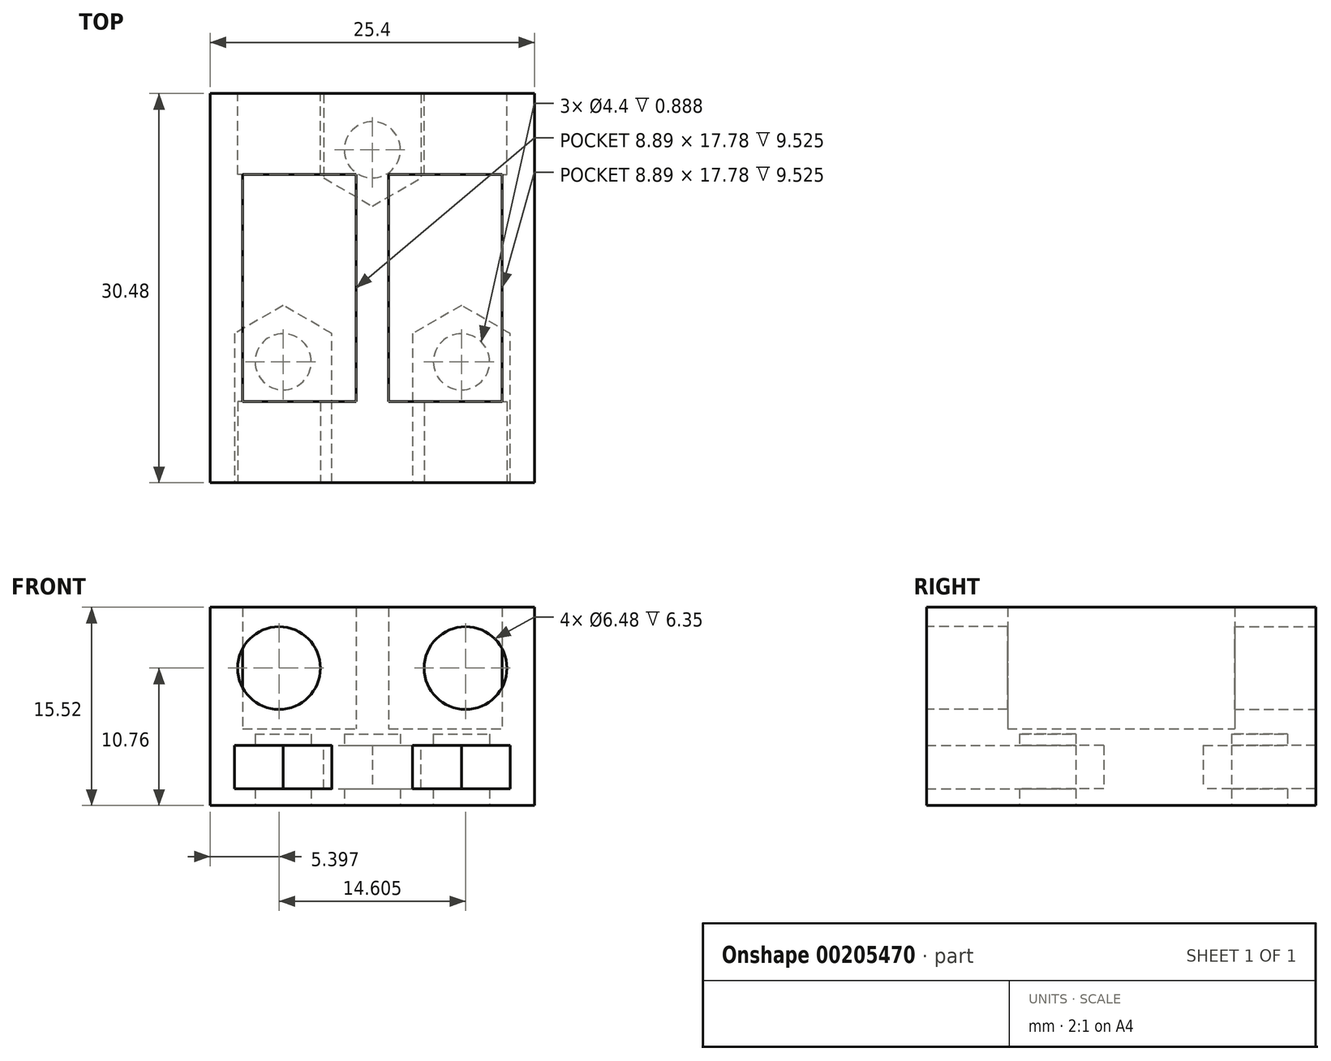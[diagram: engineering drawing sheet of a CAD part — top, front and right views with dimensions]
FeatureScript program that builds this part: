
annotation { "Feature Type Name" : "Feature", "Feature Type Description" : "" }
export const myFeature = defineFeature(function(context is Context, id is Id, definition is map)
    precondition{}
    {
        {
            var Q0;
            Q0=qCreatedBy(makeId("Front.planeOp"),FACE);
            var sketch = newSketch(context, id + "F0", { "sketchPlane" : qUnion([Q0])});
            skLineSegment(sketch, "E0.bottom", {"start": v(12.7, 4.76) * mm, "end": v(-12.7, 4.76) * mm});
            skLineSegment(sketch, "E0.top", {"start": v(12.7, -4.76) * mm, "end": v(-12.7, -4.76) * mm});
            skLineSegment(sketch, "E0.left", {"start": v(12.7, 4.76) * mm, "end": v(12.7, -4.76) * mm});
            skLineSegment(sketch, "E0.right", {"start": v(-12.7, 4.76) * mm, "end": v(-12.7, -4.76) * mm});
            skPoint(sketch, "E0.middle", {"position": v(0, 0) * mm});
            skSolve(sketch);
        }
        {
            var Q0;
            Q0=makeQuery(id+"F0.imprint","IMPRINT",FACE,{"disambiguationData":[TD([[makeQuery(id+"F0.imprint","IMPRINT",EDGE,{"derivedFrom":sQuery(id+"F0.wireOp",EDGE,"E0.bottom")}),1.0]])]});
            extrude(context, id + "F1", {"entities" : qUnion([Q0]), "depth" : 6.35 * mm});
        }
        {
            var Q0;
            Q0=makeQuery(id+"F1.opExtrude","CAP_FACE",FACE,{"disambiguationData":[OSD([sQuery(id+"F0.wireOp",EDGE,"E0.bottom"),sQuery(id+"F0.wireOp",EDGE,"E0.top"),sQuery(id+"F0.wireOp",EDGE,"E0.left"),sQuery(id+"F0.wireOp",EDGE,"E0.right")])],"isStart":false});
            var sketch = newSketch(context, id + "F2", { "sketchPlane" : qUnion([Q0])});
            skLineSegment(sketch, "E1.bottom", {"start": v(-12.7, 4.76) * mm, "end": v(-10.16, 4.76) * mm});
            skLineSegment(sketch, "E1.top", {"start": v(-12.7, -4.76) * mm, "end": v(-10.16, -4.76) * mm});
            skLineSegment(sketch, "E1.left", {"start": v(-12.7, 4.76) * mm, "end": v(-12.7, -4.76) * mm});
            skLineSegment(sketch, "E1.right", {"start": v(-10.16, 4.76) * mm, "end": v(-10.16, -4.76) * mm});
            skLineSegment(sketch, "E2.bottom", {"start": v(1.27, 4.76) * mm, "end": v(-1.27, 4.76) * mm});
            skLineSegment(sketch, "E2.top", {"start": v(1.27, -4.76) * mm, "end": v(-1.27, -4.76) * mm});
            skLineSegment(sketch, "E2.left", {"start": v(1.27, 4.76) * mm, "end": v(1.27, -4.76) * mm});
            skLineSegment(sketch, "E2.right", {"start": v(-1.27, 4.76) * mm, "end": v(-1.27, -4.76) * mm});
            skPoint(sketch, "E2.middle", {"position": v(0, 0) * mm});
            skLineSegment(sketch, "E3", {"start": v(0, 4.76) * mm, "end": v(0, -4.76) * mm, "construction": true});
            skLineSegment(sketch, "E4.MirrorCS", {"start": v(10.16, 4.76) * mm, "end": v(10.16, -4.76) * mm});
            skLineSegment(sketch, "E5.MirrorCS", {"start": v(12.7, 4.76) * mm, "end": v(12.7, -4.76) * mm});
            skLineSegment(sketch, "E6.MirrorCS", {"start": v(12.7, -4.76) * mm, "end": v(10.16, -4.76) * mm});
            skLineSegment(sketch, "E7.MirrorCS", {"start": v(12.7, 4.76) * mm, "end": v(10.16, 4.76) * mm});
            skSolve(sketch);
        }
        {
            var Q0;
            Q0 = qSketchRegion(id + "F2", true);
            extrude(context, id + "F3", {"entities" : qUnion([Q0]), "operationType" : NewBodyOperationType.ADD, "depth" : 17.78 * mm});
        }
        {
            var Q0;
            Q0=makeQuery(id+"F3.opExtrude","CAP_FACE",FACE,{"disambiguationData":[OSD([sQuery(id+"F2.wireOp",EDGE,"E1.bottom"),sQuery(id+"F2.wireOp",EDGE,"E1.top"),sQuery(id+"F2.wireOp",EDGE,"E1.left"),sQuery(id+"F2.wireOp",EDGE,"E1.right")])],"isStart":false});
            var sketch = newSketch(context, id + "F4", { "sketchPlane" : qUnion([Q0])});
            skLineSegment(sketch, "E8.bottom", {"start": v(-12.7, 4.76) * mm, "end": v(12.7, 4.76) * mm});
            skLineSegment(sketch, "E8.top", {"start": v(-12.7, -4.76) * mm, "end": v(12.7, -4.76) * mm});
            skLineSegment(sketch, "E8.left", {"start": v(-12.7, 4.76) * mm, "end": v(-12.7, -4.76) * mm});
            skLineSegment(sketch, "E8.right", {"start": v(12.7, 4.76) * mm, "end": v(12.7, -4.76) * mm});
            skSolve(sketch);
        }
        {
            var Q0;
            Q0 = qSketchRegion(id + "F4", true);
            extrude(context, id + "F5", {"entities" : qUnion([Q0]), "operationType" : NewBodyOperationType.ADD, "depth" : 6.35 * mm});
        }
        {
            var Q0;
            Q0=makeQuery(id+"F1.opExtrude","CAP_FACE",FACE,{"disambiguationData":[OSD([sQuery(id+"F0.wireOp",EDGE,"E0.bottom"),sQuery(id+"F0.wireOp",EDGE,"E0.top"),sQuery(id+"F0.wireOp",EDGE,"E0.left"),sQuery(id+"F0.wireOp",EDGE,"E0.right")])],"isStart":true});
            var sketch = newSketch(context, id + "F6", { "sketchPlane" : qUnion([Q0])});
            skCircle(sketch, "E9", {"center": v(7.3, 0) * mm, "radius": 3.24 * mm});
            skLineSegment(sketch, "E10", {"start": v(0, 4.76) * mm, "end": v(0, -4.76) * mm, "construction": true});
            skCircle(sketch, "E11.MirrorC", {"center": v(-7.3, 0) * mm, "radius": 3.24 * mm});
            skSolve(sketch);
        }
        {
            var Q0;
            Q0 = qSketchRegion(id + "F6", true);
            var Q1;
            {var subQ0=sQuery(id+"F0.wireOp",EDGE,"E0.top");var subQ1=sQuery(id+"F0.wireOp",EDGE,"E0.bottom");Q1=makeQuery(id+"F3.boolean.opBoolean","SPLIT",FACE,{"disambiguationData":[TD([makeQuery(id+"F3.opExtrude","SWEPT_FACE",FACE,{"disambiguationData":[OSD([sQuery(id+"F2.wireOp",EDGE,"E2.left")])]})])],"derivedFrom":makeQuery(id+"F1.opExtrude","CAP_FACE",FACE,{"disambiguationData":[OSD([subQ1,subQ0,sQuery(id+"F0.wireOp",EDGE,"E0.left"),sQuery(id+"F0.wireOp",EDGE,"E0.right")])],"isStart":false})});}
            extrude(context, id + "F7", {"entities" : qUnion([Q0]), "operationType" : NewBodyOperationType.REMOVE, "endBound" : BoundingType.UP_TO_SURFACE, "oppositeDirection" : true, "endBoundEntityFace" : qUnion([Q1]), "depth" : 25.4 * mm});
        }
        {
            var Q0;
            Q0=makeQuery(id+"F5.opExtrude","CAP_FACE",FACE,{"disambiguationData":[OSD([sQuery(id+"F4.wireOp",EDGE,"E8.bottom"),sQuery(id+"F4.wireOp",EDGE,"E8.top"),sQuery(id+"F4.wireOp",EDGE,"E8.left"),sQuery(id+"F4.wireOp",EDGE,"E8.right")])],"isStart":false});
            var sketch = newSketch(context, id + "F8", { "sketchPlane" : qUnion([Q0])});
            skCircle(sketch, "E12", {"center": v(-7.3, 0) * mm, "radius": 3.24 * mm});
            skCircle(sketch, "E13", {"center": v(7.3, 0) * mm, "radius": 3.24 * mm});
            skSolve(sketch);
        }
        {
            var Q0;
            Q0 = qSketchRegion(id + "F8", true);
            var Q1;
            {var subQ0=sQuery(id+"F4.wireOp",EDGE,"E8.bottom");var subQ1=sQuery(id+"F4.wireOp",EDGE,"E8.top");Q1=makeQuery(id+"F5.boolean.opBoolean","SPLIT",FACE,{"disambiguationData":[TD([makeQuery(id+"F3.opExtrude","SWEPT_FACE",FACE,{"disambiguationData":[OSD([sQuery(id+"F2.wireOp",EDGE,"E1.right")])]})])],"derivedFrom":makeQuery(id+"F5.opExtrude","CAP_FACE",FACE,{"disambiguationData":[OSD([subQ0,subQ1,sQuery(id+"F4.wireOp",EDGE,"E8.left"),sQuery(id+"F4.wireOp",EDGE,"E8.right")])],"isStart":true})});}
            extrude(context, id + "F9", {"entities" : qUnion([Q0]), "operationType" : NewBodyOperationType.REMOVE, "endBound" : BoundingType.UP_TO_SURFACE, "oppositeDirection" : true, "endBoundEntityFace" : qUnion([Q1]), "depth" : 25.4 * mm});
        }
        {
            var Q0;
            Q0=makeQuery(id+"F5.boolean.opBoolean","MERGE",FACE,{"derivedFrom":[makeQuery(id+"F3.boolean.opBoolean","MERGE",FACE,{"derivedFrom":[makeQuery(id+"F1.opExtrude","SWEPT_FACE",FACE,{"disambiguationData":[OSD([sQuery(id+"F0.wireOp",EDGE,"E0.top")])]}),makeQuery(id+"F3.opExtrude","SWEPT_FACE",FACE,{"disambiguationData":[OSD([sQuery(id+"F2.wireOp",EDGE,"E1.top")])]}),makeQuery(id+"F3.opExtrude","SWEPT_FACE",FACE,{"disambiguationData":[OSD([sQuery(id+"F2.wireOp",EDGE,"E2.top")])]}),makeQuery(id+"F3.opExtrude","SWEPT_FACE",FACE,{"disambiguationData":[OSD([sQuery(id+"F2.wireOp",EDGE,"E6.MirrorCS")])]})]}),makeQuery(id+"F5.opExtrude","SWEPT_FACE",FACE,{"disambiguationData":[OSD([sQuery(id+"F4.wireOp",EDGE,"E8.top")])]})]});
            var sketch = newSketch(context, id + "F10", { "sketchPlane" : qUnion([Q0])});
            skLineSegment(sketch, "E14.bottom", {"start": v(-12.7, 0) * mm, "end": v(12.7, 0) * mm});
            skLineSegment(sketch, "E14.top", {"start": v(-12.7, 30.48) * mm, "end": v(12.7, 30.48) * mm});
            skLineSegment(sketch, "E14.left", {"start": v(-12.7, 30.48) * mm, "end": v(-12.7, 0) * mm});
            skLineSegment(sketch, "E14.right", {"start": v(12.7, 30.48) * mm, "end": v(12.7, 0) * mm});
            skSolve(sketch);
        }
        {
            var Q0;
            Q0 = qSketchRegion(id + "F10", true);
            extrude(context, id + "F11", {"entities" : qUnion([Q0]), "operationType" : NewBodyOperationType.ADD, "depth" : 6 * mm});
        }
        {
            var Q0;
            Q0=makeQuery(id+"F11.opExtrude","CAP_FACE",FACE,{"disambiguationData":[OSD([sQuery(id+"F10.wireOp",EDGE,"E14.bottom"),sQuery(id+"F10.wireOp",EDGE,"E14.top"),sQuery(id+"F10.wireOp",EDGE,"E14.left"),sQuery(id+"F10.wireOp",EDGE,"E14.right")])],"isStart":false});
            cPlane(context, id + "F12", {"entities" : qUnion([Q0]), "cplaneType" : CPlaneType.OFFSET, "offset" : 3 * mm, "oppositeDirection" : true, "width" : 152.4 * mm, "height" : 152.4 * mm});
        }
        {
            var Q0;
            Q0=qCreatedBy(id+"F12.planeOp",FACE);
            var sketch = newSketch(context, id + "F13", { "sketchPlane" : qUnion([Q0])});
            skCircle(sketch, "E15.cCircle", {"center": v(0, 4.4) * mm, "radius": 3.82 * mm, "construction": true});
            skLineSegment(sketch, "E15.0", {"start": v(3.82, 6.61) * mm, "end": v(3.82, 2.2) * mm});
            skLineSegment(sketch, "E15.1", {"start": v(3.82, 2.2) * mm, "end": v(0, 0) * mm, "construction": true});
            skLineSegment(sketch, "E15.2", {"start": v(0, 0) * mm, "end": v(-3.82, 2.2) * mm, "construction": true});
            skLineSegment(sketch, "E15.3", {"start": v(-3.82, 2.2) * mm, "end": v(-3.82, 6.61) * mm});
            skLineSegment(sketch, "E15.4", {"start": v(-3.82, 6.61) * mm, "end": v(0, 8.82) * mm});
            skLineSegment(sketch, "E15.5", {"start": v(0, 8.82) * mm, "end": v(3.82, 6.61) * mm});
            skPoint(sketch, "E15.0.midPoint", {"position": v(3.82, 4.4) * mm});
            skCircle(sketch, "E16.cCircle", {"center": v(6.98, 21) * mm, "radius": 3.82 * mm, "construction": true});
            skLineSegment(sketch, "E16.0", {"start": v(10.8, 23.2) * mm, "end": v(10.8, 18.8) * mm});
            skLineSegment(sketch, "E16.1", {"start": v(10.8, 18.8) * mm, "end": v(6.98, 16.6) * mm});
            skLineSegment(sketch, "E16.2", {"start": v(6.98, 16.6) * mm, "end": v(3.16, 18.8) * mm});
            skLineSegment(sketch, "E16.3", {"start": v(3.16, 18.8) * mm, "end": v(3.16, 23.2) * mm});
            skLineSegment(sketch, "E16.4", {"start": v(3.16, 23.2) * mm, "end": v(6.98, 25.41) * mm, "construction": true});
            skLineSegment(sketch, "E16.5", {"start": v(6.98, 25.41) * mm, "end": v(10.8, 23.2) * mm, "construction": true});
            skPoint(sketch, "E16.0.midPoint", {"position": v(10.8, 21) * mm});
            skCircle(sketch, "E17.cCircle", {"center": v(-6.98, 21) * mm, "radius": 3.82 * mm, "construction": true});
            skLineSegment(sketch, "E17.0", {"start": v(-3.16, 23.2) * mm, "end": v(-3.16, 18.8) * mm});
            skLineSegment(sketch, "E17.1", {"start": v(-3.16, 18.8) * mm, "end": v(-6.98, 16.6) * mm});
            skLineSegment(sketch, "E17.2", {"start": v(-6.98, 16.6) * mm, "end": v(-10.8, 18.8) * mm});
            skLineSegment(sketch, "E17.3", {"start": v(-10.8, 18.8) * mm, "end": v(-10.8, 23.2) * mm});
            skLineSegment(sketch, "E17.4", {"start": v(-10.8, 23.2) * mm, "end": v(-6.98, 25.41) * mm, "construction": true});
            skLineSegment(sketch, "E17.5", {"start": v(-6.98, 25.41) * mm, "end": v(-3.16, 23.2) * mm, "construction": true});
            skPoint(sketch, "E17.0.midPoint", {"position": v(-3.16, 21) * mm});
            skLineSegment(sketch, "E18", {"start": v(-10.8, 23.2) * mm, "end": v(-10.8, 30.48) * mm});
            skLineSegment(sketch, "E19", {"start": v(-10.8, 30.48) * mm, "end": v(-3.16, 30.48) * mm});
            skLineSegment(sketch, "E20", {"start": v(-3.16, 30.48) * mm, "end": v(-3.16, 23.2) * mm});
            skLineSegment(sketch, "E21", {"start": v(3.16, 23.2) * mm, "end": v(3.16, 30.48) * mm});
            skLineSegment(sketch, "E22", {"start": v(3.16, 30.48) * mm, "end": v(10.8, 30.48) * mm});
            skLineSegment(sketch, "E23", {"start": v(10.8, 30.48) * mm, "end": v(10.8, 23.2) * mm});
            skLineSegment(sketch, "E24", {"start": v(-3.82, 2.2) * mm, "end": v(-3.82, -0.01) * mm});
            skLineSegment(sketch, "E25", {"start": v(-3.82, -0.01) * mm, "end": v(3.82, -0.01) * mm});
            skLineSegment(sketch, "E26", {"start": v(3.82, -0.01) * mm, "end": v(3.82, 2.2) * mm});
            skSolve(sketch);
        }
        {
            var Q0;
            Q0=makeQuery(id+"F13.imprint","IMPRINT",FACE,{"disambiguationData":[TD([[makeQuery(id+"F13.imprint","IMPRINT",EDGE,{"derivedFrom":sQuery(id+"F13.wireOp",EDGE,"E17.0")}),-1.0]])]});
            var Q1;
            Q1=makeQuery(id+"F13.imprint","IMPRINT",FACE,{"disambiguationData":[TD([[makeQuery(id+"F13.imprint","IMPRINT",EDGE,{"derivedFrom":sQuery(id+"F13.wireOp",EDGE,"E16.0")}),-1.0]])]});
            var Q2;
            Q2=makeQuery(id+"F13.imprint","IMPRINT",FACE,{"disambiguationData":[TD([[makeQuery(id+"F13.imprint","IMPRINT",EDGE,{"derivedFrom":sQuery(id+"F13.wireOp",EDGE,"E15.0")}),-1.0]])]});
            extrude(context, id + "F14", {"entities" : qUnion([Q0, Q1, Q2]), "operationType" : NewBodyOperationType.REMOVE, "oppositeDirection" : true, "depth" : 3.4 / 2 * mm, "hasSecondDirection" : true, "secondDirectionOppositeDirection" : false, "secondDirectionDepth" : 3.4 / 2 * mm});
        }
        {
            var Q0;
            Q0=makeQuery(id+"F11.opExtrude","CAP_FACE",FACE,{"disambiguationData":[OSD([sQuery(id+"F10.wireOp",EDGE,"E14.bottom"),sQuery(id+"F10.wireOp",EDGE,"E14.top"),sQuery(id+"F10.wireOp",EDGE,"E14.left"),sQuery(id+"F10.wireOp",EDGE,"E14.right")])],"isStart":false});
            var sketch = newSketch(context, id + "F15", { "sketchPlane" : qUnion([Q0])});
            skCircle(sketch, "E27", {"center": v(0, 4.4) * mm, "radius": 2.2 * mm});
            skCircle(sketch, "E28", {"center": v(6.98, 21) * mm, "radius": 2.2 * mm});
            skCircle(sketch, "E29", {"center": v(-6.98, 21) * mm, "radius": 2.2 * mm});
            skSolve(sketch);
        }
        {
            var Q0;
            Q0 = qSketchRegion(id + "F15", true);
            extrude(context, id + "F16", {"entities" : qUnion([Q0]), "operationType" : NewBodyOperationType.REMOVE, "oppositeDirection" : true, "depth" : 5.6 * mm});
        }
    });
